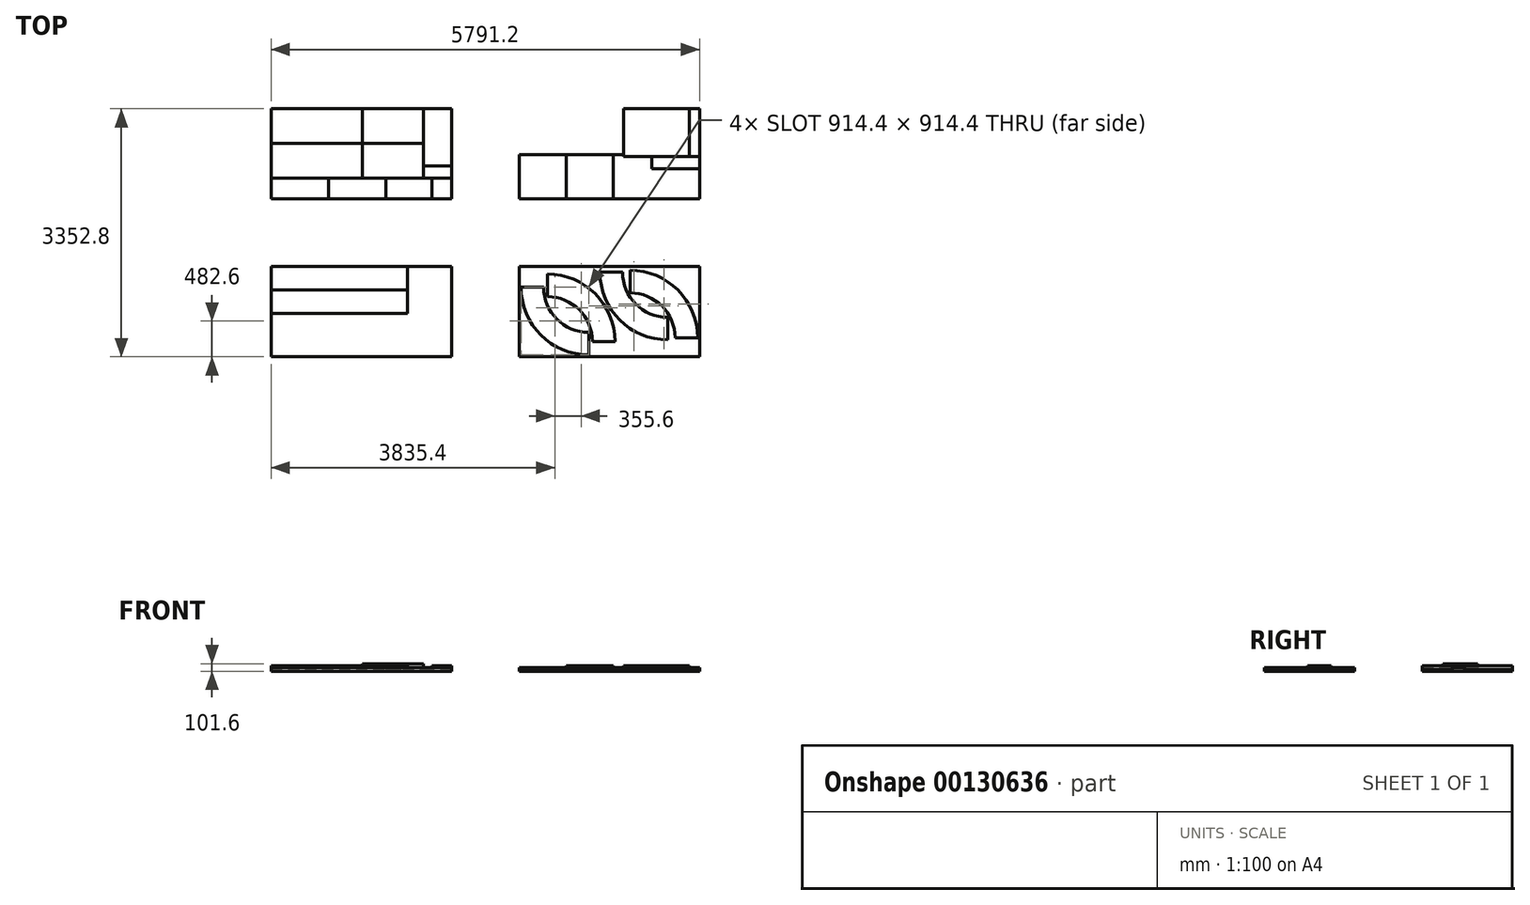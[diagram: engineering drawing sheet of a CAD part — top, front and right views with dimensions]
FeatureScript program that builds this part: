
annotation { "Feature Type Name" : "Feature", "Feature Type Description" : "" }
export const myFeature = defineFeature(function(context is Context, id is Id, definition is map)
    precondition{}
    {
        {
            var Q0;
            Q0=qCreatedBy(makeId("Top.planeOp"),FACE);
            var sketch = newSketch(context, id + "F0", { "sketchPlane" : qUnion([Q0])});
            skLineSegment(sketch, "E0.bottom", {"start": v(0, 0) * mm, "end": v(2438.4, 0) * mm});
            skLineSegment(sketch, "E0.top", {"start": v(0, 1219.2) * mm, "end": v(2438.4, 1219.2) * mm});
            skLineSegment(sketch, "E0.left", {"start": v(0, 0) * mm, "end": v(0, 1219.2) * mm});
            skLineSegment(sketch, "E0.right", {"start": v(2438.4, 0) * mm, "end": v(2438.4, 1219.2) * mm});
            skLineSegment(sketch, "E1", {"start": v(0, 901.7) * mm, "end": v(1841.5, 901.7) * mm});
            skLineSegment(sketch, "E2", {"start": v(1841.5, 901.7) * mm, "end": v(1841.5, 1219.2) * mm});
            skLineSegment(sketch, "E3", {"start": v(1841.5, 901.7) * mm, "end": v(1841.5, 584.2) * mm});
            skLineSegment(sketch, "E4", {"start": v(1841.5, 584.2) * mm, "end": v(0, 584.2) * mm});
            skLineSegment(sketch, "E5.bottom", {"start": v(3352.8, 0) * mm, "end": v(5791.2, 0) * mm});
            skLineSegment(sketch, "E5.top", {"start": v(3352.8, 1219.2) * mm, "end": v(5791.2, 1219.2) * mm});
            skLineSegment(sketch, "E5.left", {"start": v(3352.8, 0) * mm, "end": v(3352.8, 1219.2) * mm});
            skLineSegment(sketch, "E5.right", {"start": v(5791.2, 0) * mm, "end": v(5791.2, 1219.2) * mm});
            skArc(sketch, "E6", {"start": v(3378.2, 939.8) * mm, "mid": v(3646.02, 293.22) * mm, "end": v(4292.6, 25.4) * mm});
            skArc(sketch, "E7", {"start": v(3683, 939.8) * mm, "mid": v(3861.55, 508.75) * mm, "end": v(4292.6, 330.2) * mm});
            skLineSegment(sketch, "E8.trimOffspring", {"start": v(4292.6, 330.2) * mm, "end": v(4292.6, 25.4) * mm});
            skLineSegment(sketch, "E9", {"start": v(3378.2, 939.8) * mm, "end": v(3683, 939.8) * mm});
            skArc(sketch, "E10", {"start": v(4648.2, 203.2) * mm, "mid": v(4380.38, 849.78) * mm, "end": v(3733.8, 1117.6) * mm});
            skArc(sketch, "E11", {"start": v(4343.4, 203.2) * mm, "mid": v(4164.85, 634.25) * mm, "end": v(3733.8, 812.8) * mm});
            skLineSegment(sketch, "E12.trimOffspring", {"start": v(3733.8, 812.8) * mm, "end": v(3733.8, 1117.6) * mm});
            skLineSegment(sketch, "E13", {"start": v(4648.2, 203.2) * mm, "end": v(4343.4, 203.2) * mm});
            skArc(sketch, "E14", {"start": v(4445, 1143) * mm, "mid": v(4712.82, 496.42) * mm, "end": v(5359.4, 228.6) * mm});
            skArc(sketch, "E15", {"start": v(4749.8, 1143) * mm, "mid": v(4928.35, 711.95) * mm, "end": v(5359.4, 533.4) * mm});
            skLineSegment(sketch, "E16.trimOffspring", {"start": v(5359.4, 533.4) * mm, "end": v(5359.4, 228.6) * mm});
            skLineSegment(sketch, "E17", {"start": v(4445, 1143) * mm, "end": v(4749.8, 1143) * mm});
            skArc(sketch, "E18", {"start": v(5765.8, 254) * mm, "mid": v(5497.98, 900.58) * mm, "end": v(4851.4, 1168.4) * mm});
            skArc(sketch, "E19", {"start": v(5461, 254) * mm, "mid": v(5282.45, 685.05) * mm, "end": v(4851.4, 863.6) * mm});
            skLineSegment(sketch, "E20.trimOffspring", {"start": v(4851.4, 863.6) * mm, "end": v(4851.4, 1168.4) * mm});
            skLineSegment(sketch, "E21", {"start": v(5765.8, 254) * mm, "end": v(5461, 254) * mm});
            skLineSegment(sketch, "E22.bottom", {"start": v(0, 2133.6) * mm, "end": v(2438.4, 2133.6) * mm});
            skLineSegment(sketch, "E22.top", {"start": v(0, 3352.8) * mm, "end": v(2438.4, 3352.8) * mm});
            skLineSegment(sketch, "E22.left", {"start": v(0, 2133.6) * mm, "end": v(0, 3352.8) * mm});
            skLineSegment(sketch, "E22.right", {"start": v(2438.4, 2133.6) * mm, "end": v(2438.4, 3352.8) * mm});
            skLineSegment(sketch, "E23", {"start": v(0, 2882.9) * mm, "end": v(1231.9, 2882.9) * mm});
            skLineSegment(sketch, "E24", {"start": v(1231.9, 2882.9) * mm, "end": v(1231.9, 3352.8) * mm});
            skLineSegment(sketch, "E25", {"start": v(1231.9, 2882.9) * mm, "end": v(1231.9, 2413) * mm});
            skLineSegment(sketch, "E26", {"start": v(1231.9, 2413) * mm, "end": v(0, 2413) * mm});
            skLineSegment(sketch, "E27", {"start": v(774.7, 2413) * mm, "end": v(774.7, 2133.6) * mm});
            skLineSegment(sketch, "E28", {"start": v(1549.4, 2413) * mm, "end": v(1549.4, 2133.6) * mm});
            skLineSegment(sketch, "E29", {"start": v(1231.9, 2413) * mm, "end": v(1549.4, 2413) * mm});
            skLineSegment(sketch, "E30", {"start": v(1549.4, 2413) * mm, "end": v(2171.7, 2413) * mm});
            skLineSegment(sketch, "E31", {"start": v(2171.7, 2413) * mm, "end": v(2171.7, 2133.6) * mm});
            skLineSegment(sketch, "E32", {"start": v(2171.7, 2413) * mm, "end": v(2438.4, 2413) * mm});
            skLineSegment(sketch, "E33", {"start": v(1231.9, 2882.9) * mm, "end": v(2057.4, 2882.9) * mm});
            skLineSegment(sketch, "E34", {"start": v(2057.4, 2882.9) * mm, "end": v(2057.4, 2413) * mm});
            skLineSegment(sketch, "E35", {"start": v(2057.4, 2882.9) * mm, "end": v(2057.4, 3352.8) * mm});
            skLineSegment(sketch, "E36", {"start": v(2057.4, 2578.1) * mm, "end": v(2438.4, 2578.1) * mm});
            skLineSegment(sketch, "E37.bottom", {"start": v(3352.8, 2133.6) * mm, "end": v(5791.2, 2133.6) * mm});
            skLineSegment(sketch, "E37.top", {"start": v(3352.8, 3352.8) * mm, "end": v(5791.2, 3352.8) * mm});
            skLineSegment(sketch, "E37.left", {"start": v(3352.8, 2133.6) * mm, "end": v(3352.8, 3352.8) * mm});
            skLineSegment(sketch, "E37.right", {"start": v(5791.2, 2133.6) * mm, "end": v(5791.2, 3352.8) * mm});
            skLineSegment(sketch, "E38", {"start": v(3352.8, 2730.5) * mm, "end": v(4762.5, 2730.5) * mm});
            skLineSegment(sketch, "E39", {"start": v(4762.5, 2730.5) * mm, "end": v(4762.5, 3352.8) * mm});
            skLineSegment(sketch, "E40", {"start": v(4762.5, 2730.5) * mm, "end": v(4762.5, 2705.1) * mm});
            skLineSegment(sketch, "E41", {"start": v(4762.5, 2705.1) * mm, "end": v(5791.2, 2705.1) * mm});
            skLineSegment(sketch, "E42", {"start": v(5651.5, 2705.1) * mm, "end": v(5651.5, 3352.8) * mm});
            skLineSegment(sketch, "E43", {"start": v(5651.5, 3352.8) * mm, "end": v(5791.2, 3352.8) * mm});
            skLineSegment(sketch, "E44", {"start": v(3352.8, 2730.5) * mm, "end": v(3352.8, 2133.6) * mm});
            skLineSegment(sketch, "E45", {"start": v(3352.8, 2133.6) * mm, "end": v(3987.8, 2133.6) * mm});
            skLineSegment(sketch, "E46", {"start": v(3987.8, 2133.6) * mm, "end": v(3987.8, 2730.5) * mm});
            skLineSegment(sketch, "E47", {"start": v(4622.8, 2730.5) * mm, "end": v(4622.8, 2133.6) * mm});
            skLineSegment(sketch, "E48", {"start": v(5791.2, 2540) * mm, "end": v(5143.5, 2540) * mm});
            skLineSegment(sketch, "E49", {"start": v(5143.5, 2540) * mm, "end": v(5143.5, 2705.1) * mm});
            skSolve(sketch);
        }
        {
            var Q0;
            {var subQ4=sQuery(id+"F0.wireOp",EDGE,"E23");Q0=makeQuery(id+"F0.imprint","IMPRINT",FACE,{"disambiguationData":[TD([[makeQuery(id+"F0.imprint","IMPRINT",EDGE,{"derivedFrom":subQ4}),1.0]])]});}
            var Q1;
            {var subQ3=sQuery(id+"F0.wireOp",EDGE,"E27");Q1=makeQuery(id+"F0.imprint","IMPRINT",FACE,{"disambiguationData":[TD([[makeQuery(id+"F0.imprint","IMPRINT",EDGE,{"derivedFrom":subQ3}),-1.0]])]});}
            var Q2;
            {var subQ1=sQuery(id+"F0.wireOp",EDGE,"E28");Q2=makeQuery(id+"F0.imprint","IMPRINT",FACE,{"disambiguationData":[TD([[makeQuery(id+"F0.imprint","IMPRINT",EDGE,{"derivedFrom":subQ1}),1.0]])]});}
            var Q3;
            {var subQ0=sQuery(id+"F0.wireOp",EDGE,"E35");Q3=makeQuery(id+"F0.imprint","IMPRINT",FACE,{"disambiguationData":[TD([[makeQuery(id+"F0.imprint","IMPRINT",EDGE,{"derivedFrom":subQ0}),-1.0]])]});}
            var Q4;
            {var subQ4=sQuery(id+"F0.wireOp",EDGE,"E1");Q4=makeQuery(id+"F0.imprint","IMPRINT",FACE,{"disambiguationData":[TD([[makeQuery(id+"F0.imprint","IMPRINT",EDGE,{"derivedFrom":subQ4}),1.0]])]});}
            var Q5;
            {var subQ0=sQuery(id+"F0.wireOp",EDGE,"E44");Q5=makeQuery(id+"F0.imprint","IMPRINT",FACE,{"disambiguationData":[TD([[makeQuery(id+"F0.imprint","IMPRINT",EDGE,{"derivedFrom":subQ0}),1.0]])]});}
            var Q6;
            {var subQ0=sQuery(id+"F0.wireOp",EDGE,"E40");Q6=makeQuery(id+"F0.imprint","IMPRINT",FACE,{"disambiguationData":[TD([[makeQuery(id+"F0.imprint","IMPRINT",EDGE,{"derivedFrom":subQ0}),-1.0]])]});}
            var Q7;
            {var subQ4=sQuery(id+"F0.wireOp",EDGE,"E42");Q7=makeQuery(id+"F0.imprint","IMPRINT",FACE,{"disambiguationData":[TD([[makeQuery(id+"F0.imprint","IMPRINT",EDGE,{"derivedFrom":subQ4}),-1.0]])]});}
            var Q8;
            Q8=makeQuery(id+"F0.imprint","IMPRINT",FACE,{"disambiguationData":[TD([[makeQuery(id+"F0.imprint","IMPRINT",EDGE,{"derivedFrom":sQuery(id+"F0.wireOp",EDGE,"E5.bottom")}),1.0]])]});
            extrude(context, id + "F1", {"entities" : qUnion([Q0, Q1, Q2, Q3, Q4, Q5, Q6, Q7, Q8]), "depth" : 25.4 * mm});
        }
        {
            var Q0;
            {var subQ3=sQuery(id+"F0.wireOp",EDGE,"E23");Q0=makeQuery(id+"F0.imprint","IMPRINT",FACE,{"disambiguationData":[TD([[makeQuery(id+"F0.imprint","IMPRINT",EDGE,{"derivedFrom":subQ3}),-1.0]])]});}
            var Q1;
            {var subQ0=sQuery(id+"F0.wireOp",EDGE,"E32");Q1=makeQuery(id+"F0.imprint","IMPRINT",FACE,{"disambiguationData":[TD([[makeQuery(id+"F0.imprint","IMPRINT",EDGE,{"derivedFrom":subQ0}),1.0]])]});}
            var Q2;
            {var subQ2=sQuery(id+"F0.wireOp",EDGE,"E0.bottom");Q2=makeQuery(id+"F0.imprint","IMPRINT",FACE,{"disambiguationData":[TD([[makeQuery(id+"F0.imprint","IMPRINT",EDGE,{"derivedFrom":subQ2}),1.0]])]});}
            var Q3;
            {var subQ3=sQuery(id+"F0.wireOp",EDGE,"E37.left");Q3=makeQuery(id+"F0.imprint","IMPRINT",FACE,{"disambiguationData":[TD([[makeQuery(id+"F0.imprint","IMPRINT",EDGE,{"derivedFrom":subQ3}),-1.0]])]});}
            var Q4;
            {var subQ0=sQuery(id+"F0.wireOp",EDGE,"E48");Q4=makeQuery(id+"F0.imprint","IMPRINT",FACE,{"disambiguationData":[TD([[makeQuery(id+"F0.imprint","IMPRINT",EDGE,{"derivedFrom":subQ0}),-1.0]])]});}
            var Q5;
            Q5=makeQuery(id+"F0.imprint","IMPRINT",FACE,{"disambiguationData":[TD([[makeQuery(id+"F0.imprint","IMPRINT",EDGE,{"derivedFrom":sQuery(id+"F0.wireOp",EDGE,"E6")}),1.0]])]});
            var Q6;
            Q6=makeQuery(id+"F0.imprint","IMPRINT",FACE,{"disambiguationData":[TD([[makeQuery(id+"F0.imprint","IMPRINT",EDGE,{"derivedFrom":sQuery(id+"F0.wireOp",EDGE,"E10")}),1.0]])]});
            var Q7;
            Q7=makeQuery(id+"F0.imprint","IMPRINT",FACE,{"disambiguationData":[TD([[makeQuery(id+"F0.imprint","IMPRINT",EDGE,{"derivedFrom":sQuery(id+"F0.wireOp",EDGE,"E14")}),1.0]])]});
            var Q8;
            Q8=makeQuery(id+"F0.imprint","IMPRINT",FACE,{"disambiguationData":[TD([[makeQuery(id+"F0.imprint","IMPRINT",EDGE,{"derivedFrom":sQuery(id+"F0.wireOp",EDGE,"E18")}),1.0]])]});
            extrude(context, id + "F2", {"entities" : qUnion([Q0, Q1, Q2, Q3, Q4, Q5, Q6, Q7, Q8]), "depth" : 50.8 * mm});
        }
        {
            var Q0;
            {var subQ0=sQuery(id+"F0.wireOp",EDGE,"E24");Q0=makeQuery(id+"F0.imprint","IMPRINT",FACE,{"disambiguationData":[TD([[makeQuery(id+"F0.imprint","IMPRINT",EDGE,{"derivedFrom":subQ0}),-1.0]])]});}
            var Q1;
            {var subQ1=sQuery(id+"F0.wireOp",EDGE,"E27");Q1=makeQuery(id+"F0.imprint","IMPRINT",FACE,{"disambiguationData":[TD([[makeQuery(id+"F0.imprint","IMPRINT",EDGE,{"derivedFrom":subQ1}),1.0]])]});}
            var Q2;
            {var subQ3=sQuery(id+"F0.wireOp",EDGE,"E31");Q2=makeQuery(id+"F0.imprint","IMPRINT",FACE,{"disambiguationData":[TD([[makeQuery(id+"F0.imprint","IMPRINT",EDGE,{"derivedFrom":subQ3}),1.0]])]});}
            var Q3;
            {var subQ0=sQuery(id+"F0.wireOp",EDGE,"E1");Q3=makeQuery(id+"F0.imprint","IMPRINT",FACE,{"disambiguationData":[TD([[makeQuery(id+"F0.imprint","IMPRINT",EDGE,{"derivedFrom":subQ0}),-1.0]])]});}
            var Q4;
            {var subQ0=sQuery(id+"F0.wireOp",EDGE,"E46");Q4=makeQuery(id+"F0.imprint","IMPRINT",FACE,{"disambiguationData":[TD([[makeQuery(id+"F0.imprint","IMPRINT",EDGE,{"derivedFrom":subQ0}),-1.0]])]});}
            var Q5;
            {var subQ3=sQuery(id+"F0.wireOp",EDGE,"E39");Q5=makeQuery(id+"F0.imprint","IMPRINT",FACE,{"disambiguationData":[TD([[makeQuery(id+"F0.imprint","IMPRINT",EDGE,{"derivedFrom":subQ3}),-1.0]])]});}
            extrude(context, id + "F3", {"entities" : qUnion([Q0, Q1, Q2, Q3, Q4, Q5]), "depth" : 76.2 * mm});
        }
        {
            var Q0;
            Q0=makeQuery(id+"F0.imprint","IMPRINT",FACE,{"disambiguationData":[TD([[makeQuery(id+"F0.imprint","IMPRINT",EDGE,{"derivedFrom":sQuery(id+"F0.wireOp",EDGE,"E25")}),1.0]])]});
            extrude(context, id + "F4", {"entities" : qUnion([Q0]), "depth" : 101.6 * mm});
        }
    });
